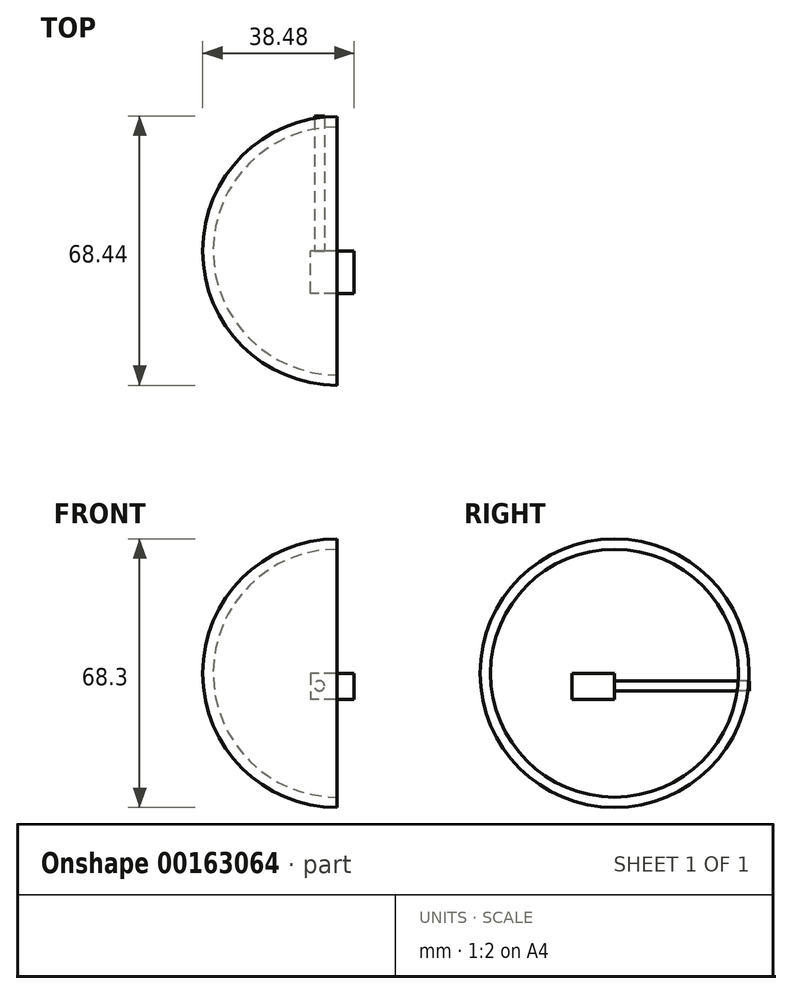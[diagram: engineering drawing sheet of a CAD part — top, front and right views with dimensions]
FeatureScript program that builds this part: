
annotation { "Feature Type Name" : "Feature", "Feature Type Description" : "" }
export const myFeature = defineFeature(function(context is Context, id is Id, definition is map)
    precondition{}
    {
        {
            var Q0;
            Q0=qCreatedBy(makeId("Top.planeOp"),FACE);
            var sketch = newSketch(context, id + "F0", { "sketchPlane" : qUnion([Q0])});
            skArc(sketch, "E0", {"start": v(-36.8, 34.15) * mm, "mid": v(-70.95, 0) * mm, "end": v(-36.8, -34.15) * mm});
            skPoint(sketch, "E1.end.orphan", {"position": v(-36.8, -34.15) * mm});
            skLineSegment(sketch, "E2", {"start": v(-36.8, -34.15) * mm, "end": v(-36.8, 34.15) * mm});
            skLineSegment(sketch, "E3", {"start": v(-36.8, 45.94) * mm, "end": v(-36.8, -63.8) * mm});
            skArc(sketch, "E4", {"start": v(-36.8, 31.5) * mm, "mid": v(-68.3, 0) * mm, "end": v(-36.8, -31.5) * mm});
            skSolve(sketch);
        }
        {
            var Q0;
            Q0=qCreatedBy(makeId("Front.planeOp"),FACE);
            var sketch = newSketch(context, id + "F1", { "sketchPlane" : qUnion([Q0])});
            skLineSegment(sketch, "E5.bottom", {"start": v(-32.47, 0) * mm, "end": v(-43.52, 0) * mm});
            skLineSegment(sketch, "E5.top", {"start": v(-32.47, -6.7) * mm, "end": v(-43.52, -6.7) * mm});
            skLineSegment(sketch, "E5.left", {"start": v(-32.47, 0) * mm, "end": v(-32.47, -6.7) * mm});
            skLineSegment(sketch, "E5.right", {"start": v(-43.52, 0) * mm, "end": v(-43.52, -6.7) * mm});
            skSolve(sketch);
        }
        {
            var Q0;
            {var subQ0=sQuery(id+"F0.wireOp",EDGE,"E0");Q0=makeQuery(id+"F0.imprint","IMPRINT",FACE,{"disambiguationData":[TD([[makeQuery(id+"F0.imprint","IMPRINT",EDGE,{"derivedFrom":subQ0}),1.0]])]});}
            var Q1;
            Q1=sQuery(id+"F0.wireOp",EDGE,"E3");
            revolve(context, id + "F2", {"entities" : qUnion([Q0]), "axis" : qUnion([Q1]), "revolveType" : RevolveType.SYMMETRIC, "angle" : 180 * degree});
        }
        {
            var Q0;
            Q0 = qSketchRegion(id + "F1", true);
            extrude(context, id + "F3", {"entities" : qUnion([Q0]), "depth" : 10.8 * mm});
        }
        {
            var Q0;
            Q0=makeQuery(id+"F3.opExtrude","CAP_FACE",FACE,{"disambiguationData":[OSD([sQuery(id+"F1.wireOp",EDGE,"E5.bottom"),sQuery(id+"F1.wireOp",EDGE,"E5.top"),sQuery(id+"F1.wireOp",EDGE,"E5.left"),sQuery(id+"F1.wireOp",EDGE,"E5.right")])],"isStart":true});
            var sketch = newSketch(context, id + "F4", { "sketchPlane" : qUnion([Q0])});
            skCircle(sketch, "E6", {"center": v(41.3, -3.21) * mm, "radius": 1.29 * mm});
            skSolve(sketch);
        }
        {
            var Q0;
            Q0 = qSketchRegion(id + "F4", true);
            extrude(context, id + "F5", {"entities" : qUnion([Q0]), "depth" : 34.3 * mm});
        }
    });
